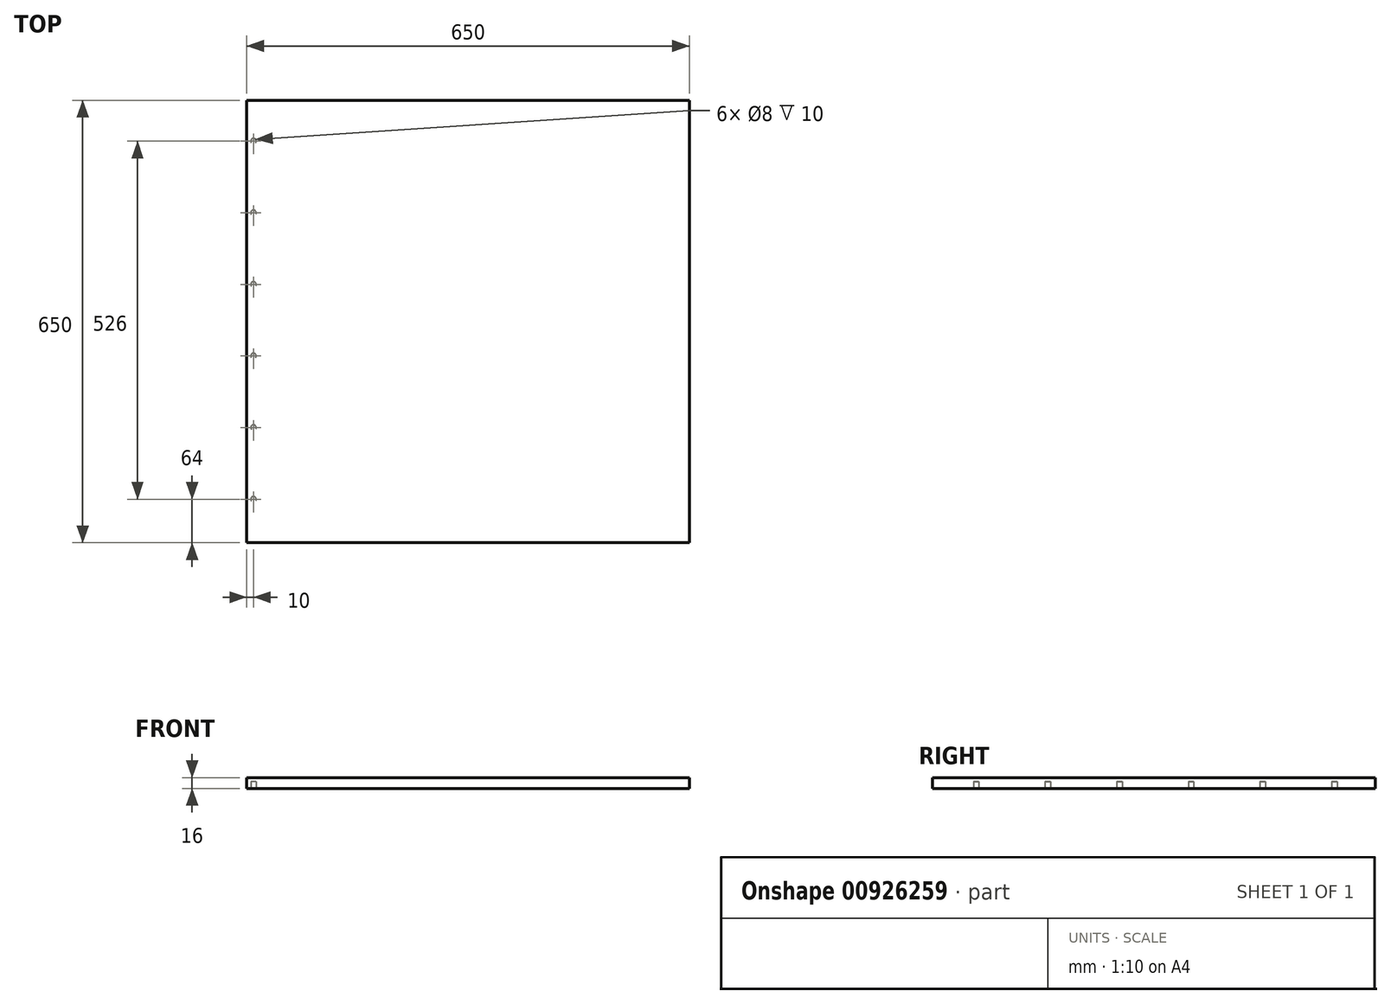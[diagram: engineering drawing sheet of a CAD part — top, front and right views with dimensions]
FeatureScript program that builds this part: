
annotation { "Feature Type Name" : "Feature", "Feature Type Description" : "" }
export const myFeature = defineFeature(function(context is Context, id is Id, definition is map)
    precondition{}
    {
        {
            var Q0;
            Q0=qCreatedBy(makeId("Top.planeOp"),FACE);
            var sketch = newSketch(context, id + "F0", { "sketchPlane" : qUnion([Q0])});
            skLineSegment(sketch, "E0.bottom", {"start": v(325, -325) * mm, "end": v(-325, -325) * mm});
            skLineSegment(sketch, "E0.top", {"start": v(325, 325) * mm, "end": v(-325, 325) * mm});
            skLineSegment(sketch, "E0.left", {"start": v(325, -325) * mm, "end": v(325, 325) * mm});
            skLineSegment(sketch, "E0.right", {"start": v(-325, -325) * mm, "end": v(-325, 325) * mm});
            skPoint(sketch, "E0.middle", {"position": v(0, 0) * mm});
            skLineSegment(sketch, "E1.bottom", {"start": v(305, 305) * mm, "end": v(-305, 305) * mm, "construction": true});
            skLineSegment(sketch, "E1.top", {"start": v(305, -305) * mm, "end": v(-305, -305) * mm, "construction": true});
            skLineSegment(sketch, "E1.left", {"start": v(305, 305) * mm, "end": v(305, -305) * mm, "construction": true});
            skLineSegment(sketch, "E1.right", {"start": v(-305, 305) * mm, "end": v(-305, -305) * mm, "construction": true});
            skLineSegment(sketch, "E2", {"start": v(-305, 305) * mm, "end": v(-325, 305) * mm, "construction": true});
            skLineSegment(sketch, "E3", {"start": v(-305, -305) * mm, "end": v(-325, -305) * mm, "construction": true});
            skLineSegment(sketch, "E4", {"start": v(-315, -305) * mm, "end": v(-315, 305) * mm, "construction": true});
            skCircle(sketch, "E5", {"center": v(-315, 265) * mm, "radius": 4 * mm});
            skCircle(sketch, "E6.0.1.0", {"center": v(-315, 159.8) * mm, "radius": 4 * mm});
            skCircle(sketch, "E6.0.2.0", {"center": v(-315, 54.6) * mm, "radius": 4 * mm});
            skCircle(sketch, "E6.0.3.0", {"center": v(-315, -50.6) * mm, "radius": 4 * mm});
            skCircle(sketch, "E6.0.4.0", {"center": v(-315, -155.8) * mm, "radius": 4 * mm});
            skCircle(sketch, "E6.0.5.0", {"center": v(-315, -261) * mm, "radius": 4 * mm});
            skLineSegment(sketch, "E6.direction1", {"start": v(-315, 265) * mm, "end": v(-290, 265) * mm, "construction": true});
            skLineSegment(sketch, "E6.direction2", {"start": v(-315, 265) * mm, "end": v(-315, 159.8) * mm, "construction": true});
            skSolve(sketch);
        }
        {
            var Q0;
            Q0=makeQuery(id+"F0.imprint","IMPRINT",FACE,{"disambiguationData":[TD([[makeQuery(id+"F0.imprint","IMPRINT",EDGE,{"derivedFrom":sQuery(id+"F0.wireOp",EDGE,"E0.bottom")}),-1.0]])]});
            var Q1;
            Q1=makeQuery(id+"F0.imprint","IMPRINT",FACE,{"disambiguationData":[TD([[makeQuery(id+"F0.imprint","IMPRINT",EDGE,{"derivedFrom":sQuery(id+"F0.wireOp",EDGE,"E5")}),1.0]])]});
            var Q2;
            Q2=makeQuery(id+"F0.imprint","IMPRINT",FACE,{"disambiguationData":[TD([[makeQuery(id+"F0.imprint","IMPRINT",EDGE,{"derivedFrom":sQuery(id+"F0.wireOp",EDGE,"E6.0.1.0")}),1.0]])]});
            var Q3;
            Q3=makeQuery(id+"F0.imprint","IMPRINT",FACE,{"disambiguationData":[TD([[makeQuery(id+"F0.imprint","IMPRINT",EDGE,{"derivedFrom":sQuery(id+"F0.wireOp",EDGE,"E6.0.2.0")}),1.0]])]});
            var Q4;
            Q4=makeQuery(id+"F0.imprint","IMPRINT",FACE,{"disambiguationData":[TD([[makeQuery(id+"F0.imprint","IMPRINT",EDGE,{"derivedFrom":sQuery(id+"F0.wireOp",EDGE,"E6.0.3.0")}),1.0]])]});
            var Q5;
            Q5=makeQuery(id+"F0.imprint","IMPRINT",FACE,{"disambiguationData":[TD([[makeQuery(id+"F0.imprint","IMPRINT",EDGE,{"derivedFrom":sQuery(id+"F0.wireOp",EDGE,"E6.0.4.0")}),1.0]])]});
            var Q6;
            Q6=makeQuery(id+"F0.imprint","IMPRINT",FACE,{"disambiguationData":[TD([[makeQuery(id+"F0.imprint","IMPRINT",EDGE,{"derivedFrom":sQuery(id+"F0.wireOp",EDGE,"E6.0.5.0")}),1.0]])]});
            extrude(context, id + "F1", {"entities" : qUnion([Q0, Q1, Q2, Q3, Q4, Q5, Q6]), "depth" : 16 * mm, "offsetDistance" : 25 * mm});
        }
        {
            var Q0;
            Q0=makeQuery(id+"F0.imprint","IMPRINT",FACE,{"disambiguationData":[TD([[makeQuery(id+"F0.imprint","IMPRINT",EDGE,{"derivedFrom":sQuery(id+"F0.wireOp",EDGE,"E5")}),1.0]])]});
            var Q1;
            Q1=makeQuery(id+"F0.imprint","IMPRINT",FACE,{"disambiguationData":[TD([[makeQuery(id+"F0.imprint","IMPRINT",EDGE,{"derivedFrom":sQuery(id+"F0.wireOp",EDGE,"E6.0.1.0")}),1.0]])]});
            var Q2;
            Q2=makeQuery(id+"F0.imprint","IMPRINT",FACE,{"disambiguationData":[TD([[makeQuery(id+"F0.imprint","IMPRINT",EDGE,{"derivedFrom":sQuery(id+"F0.wireOp",EDGE,"E6.0.2.0")}),1.0]])]});
            var Q3;
            Q3=makeQuery(id+"F0.imprint","IMPRINT",FACE,{"disambiguationData":[TD([[makeQuery(id+"F0.imprint","IMPRINT",EDGE,{"derivedFrom":sQuery(id+"F0.wireOp",EDGE,"E6.0.3.0")}),1.0]])]});
            var Q4;
            Q4=makeQuery(id+"F0.imprint","IMPRINT",FACE,{"disambiguationData":[TD([[makeQuery(id+"F0.imprint","IMPRINT",EDGE,{"derivedFrom":sQuery(id+"F0.wireOp",EDGE,"E6.0.4.0")}),1.0]])]});
            var Q5;
            Q5=makeQuery(id+"F0.imprint","IMPRINT",FACE,{"disambiguationData":[TD([[makeQuery(id+"F0.imprint","IMPRINT",EDGE,{"derivedFrom":sQuery(id+"F0.wireOp",EDGE,"E6.0.5.0")}),1.0]])]});
            extrude(context, id + "F2", {"entities" : qUnion([Q0, Q1, Q2, Q3, Q4, Q5]), "operationType" : NewBodyOperationType.REMOVE, "depth" : 10 * mm, "offsetDistance" : 25 * mm});
        }
    });
